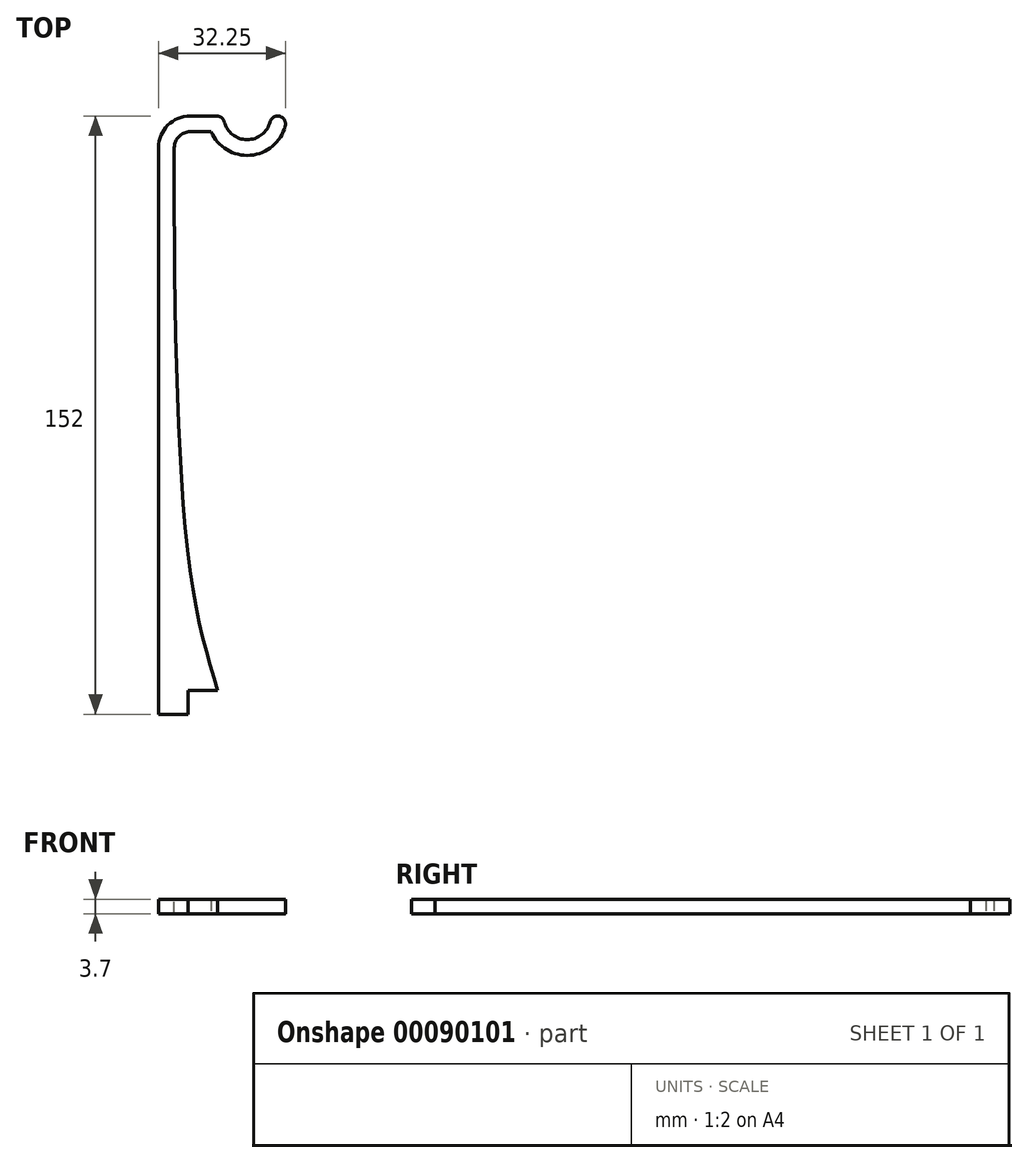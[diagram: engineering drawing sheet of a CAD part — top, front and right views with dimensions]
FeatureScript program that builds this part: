
annotation { "Feature Type Name" : "Feature", "Feature Type Description" : "" }
export const myFeature = defineFeature(function(context is Context, id is Id, definition is map)
    precondition{}
    {
        {
            var Q0;
            Q0=qCreatedBy(makeId("Top.planeOp"),FACE);
            var sketch = newSketch(context, id + "F0", { "sketchPlane" : qUnion([Q0])});
            skLineSegment(sketch, "E0", {"start": v(0, 0) * mm, "end": v(0, 138) * mm});
            skArc(sketch, "E1", {"start": v(16.7, 144.5) * mm, "mid": v(22.5, 140) * mm, "end": v(28.3, 144.5) * mm});
            skLineSegment(sketch, "E2", {"start": v(14.75, 146) * mm, "end": v(8, 146) * mm});
            skArc(sketch, "E3.0", {"start": v(13.33, 142) * mm, "mid": v(23.3, 136.03) * mm, "end": v(32.18, 143.5) * mm});
            skLineSegment(sketch, "E4", {"start": v(7.99, 142) * mm, "end": v(13.33, 142) * mm});
            skLineSegment(sketch, "E5", {"start": v(0, 0) * mm, "end": v(7.5, 0) * mm});
            skLineSegment(sketch, "E6", {"start": v(7.5, 0) * mm, "end": v(15, 0) * mm});
            skFitSpline(sketch, "E7", {"points": [v(4, 142) * mm, v(7.78, 32.09) * mm, v(15, 0) * mm], "startDerivative": vector(-0.68, -185.8) * mm, "endDerivative": vector(22.88, -75.96) * mm});
            skLineSegment(sketch, "E8", {"start": v(30.25, 146) * mm, "end": v(30.25, 146) * mm});
            skLineSegment(sketch, "E9.top", {"start": v(0, -6) * mm, "end": v(7.5, -6) * mm});
            skLineSegment(sketch, "E9.left", {"start": v(0, 0) * mm, "end": v(0, -6) * mm});
            skLineSegment(sketch, "E9.right", {"start": v(7.5, 0) * mm, "end": v(7.5, -6) * mm});
            skPoint(sketch, "E10.visualSharp", {"position": v(16.5, 146) * mm});
            skArc(sketch, "E10.filletArc", {"start": v(16.7, 144.5) * mm, "mid": v(15.98, 145.58) * mm, "end": v(14.75, 146) * mm});
            skPoint(sketch, "E11.visualSharp", {"position": v(28.5, 146) * mm});
            skArc(sketch, "E11.filletArc", {"start": v(30.25, 146) * mm, "mid": v(29.02, 145.58) * mm, "end": v(28.3, 144.5) * mm});
            skPoint(sketch, "E12.visualSharp", {"position": v(32.5, 146) * mm});
            skArc(sketch, "E12.filletArc", {"start": v(32.18, 143.5) * mm, "mid": v(31.83, 145.22) * mm, "end": v(30.25, 146) * mm});
            skArc(sketch, "E13.filletArc", {"start": v(7.99, 142) * mm, "mid": v(5.16, 140.83) * mm, "end": v(3.99, 138) * mm});
            skPoint(sketch, "E14.visualSharp", {"position": v(0, 146) * mm});
            skArc(sketch, "E14.filletArc", {"start": v(8, 146) * mm, "mid": v(2.34, 143.66) * mm, "end": v(0, 138) * mm});
            skSolve(sketch);
        }
        {
            var Q0;
            Q0=makeQuery(id+"F0.imprint","IMPRINT",FACE,{"disambiguationData":[TD([[makeQuery(id+"F0.imprint","IMPRINT",EDGE,{"derivedFrom":sQuery(id+"F0.wireOp",EDGE,"E5")}),-1.0]])]});
            var Q1;
            Q1=makeQuery(id+"F0.imprint","IMPRINT",FACE,{"disambiguationData":[TD([[makeQuery(id+"F0.imprint","IMPRINT",EDGE,{"derivedFrom":sQuery(id+"F0.wireOp",EDGE,"E0")}),-1.0]])]});
            extrude(context, id + "F1", {"entities" : qUnion([Q0, Q1]), "depth" : 3.7 * mm});
        }
    });
